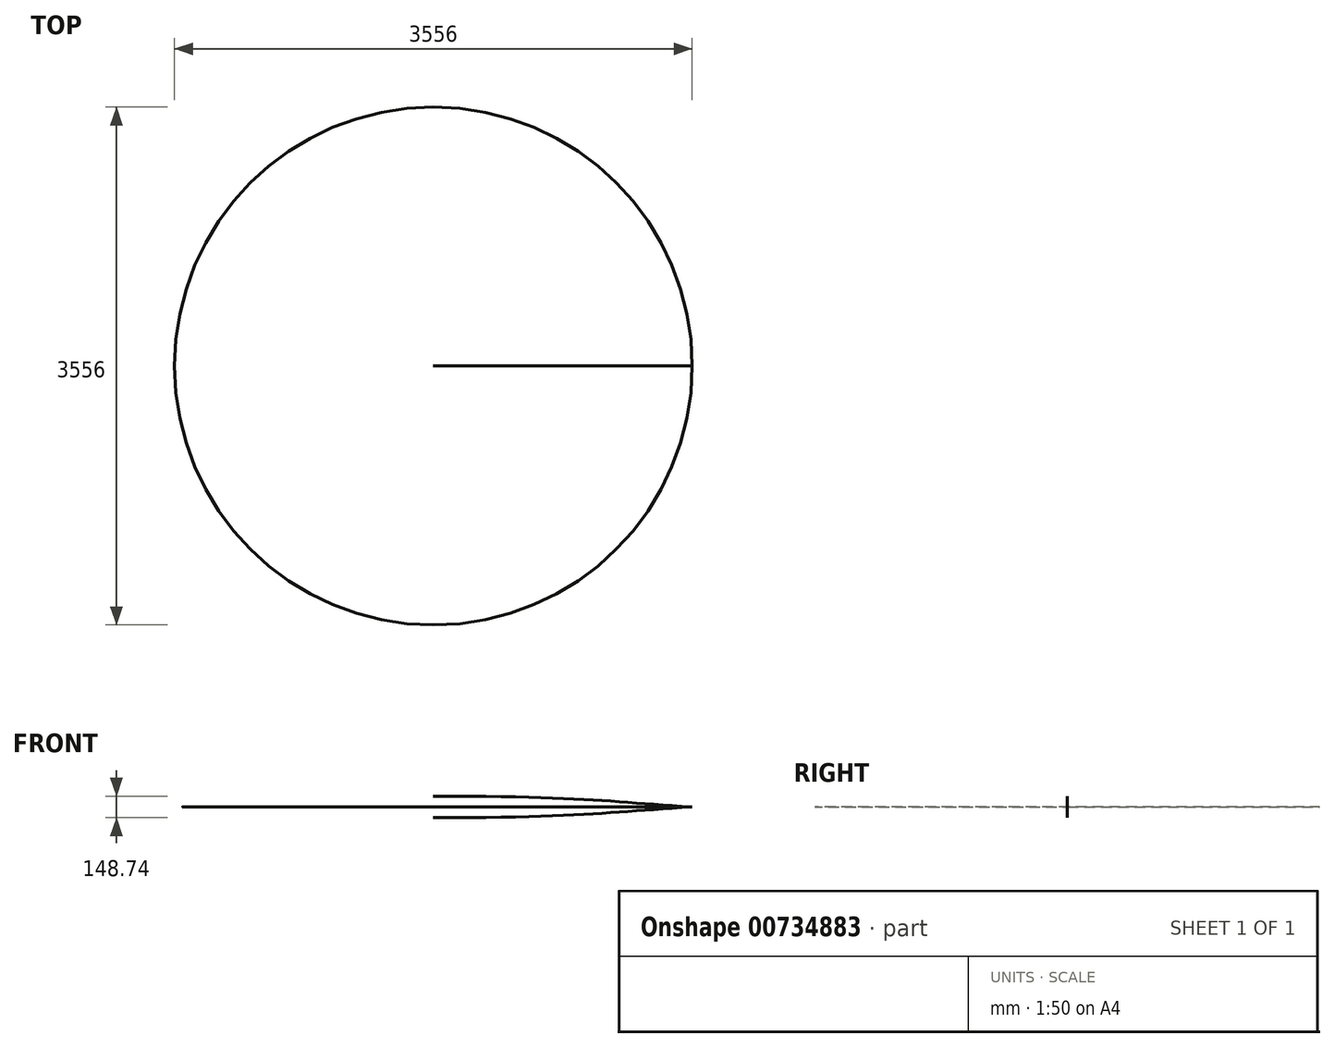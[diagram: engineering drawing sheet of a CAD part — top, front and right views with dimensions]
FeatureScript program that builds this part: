
annotation { "Feature Type Name" : "Feature", "Feature Type Description" : "" }
export const myFeature = defineFeature(function(context is Context, id is Id, definition is map)
    precondition{}
    {
        {
            var Q0;
            Q0=qCreatedBy(makeId("Front.planeOp"),FACE);
            var sketch = newSketch(context, id + "F0", { "sketchPlane" : qUnion([Q0])});
            skLineSegment(sketch, "E0", {"start": v(0, 45.77) * mm, "end": v(0, -49.43) * mm});
            skSolve(sketch);
        }
        {
            var Q0;
            Q0=qCreatedBy(makeId("Front.planeOp"),FACE);
            var sketch = newSketch(context, id + "F1", { "sketchPlane" : qUnion([Q0])});
            skFitSpline(sketch, "E1", {"points": [v(1778, 0) * mm, v(0, 74.37) * mm], "startDerivative": vector(-1668.8, 99.33) * mm, "endDerivative": vector(-3075.44, 0) * mm});
            skFitSpline(sketch, "E2.MirrorCS", {"points": [v(1778, 0) * mm, v(0, -74.37) * mm], "startDerivative": vector(-1668.8, -99.33) * mm, "endDerivative": vector(-3075.44, 0) * mm});
            skLineSegment(sketch, "E3", {"start": v(0, 74.37) * mm, "end": v(0, -74.37) * mm});
            skSolve(sketch);
        }
        {
            var Q0;
            Q0=makeQuery(id+"F1.imprint","IMPRINT",FACE,{"disambiguationData":[TD([[makeQuery(id+"F1.imprint","IMPRINT",EDGE,{"derivedFrom":sQuery(id+"F1.wireOp",EDGE,"E1")}),1.0]])]});
            var Q1;
            Q1=sQuery(id+"F1.wireOp",EDGE,"E1");
            var Q2;
            Q2=sQuery(id+"F1.wireOp",EDGE,"E2.MirrorCS");
            var Q3;
            Q3=sQuery(id+"F0.wireOp",EDGE,"E0");
            revolve(context, id + "F2", {"surfaceOperationType" : NewSurfaceOperationType.NEW, "entities" : qUnion([Q0]), "surfaceEntities" : qUnion([Q1, Q2]), "axis" : qUnion([Q3]), "revolveType" : RevolveType.FULL});
        }
        {
            var Q0;
            Q0=qCreatedBy(makeId("Top.planeOp"),FACE);
            var sketch = newSketch(context, id + "F3", { "sketchPlane" : qUnion([Q0])});
            skLineSegment(sketch, "E4", {"start": v(0, 1845.71) * mm, "end": v(0, -1890.02) * mm, "construction": true});
            skLineSegment(sketch, "E5", {"start": v(0, 0) * mm, "end": v(1614.14, 931.92) * mm, "construction": true});
            skLineSegment(sketch, "E6", {"start": v(0, 0) * mm, "end": v(-1636.2, 944.66) * mm, "construction": true});
            skCircle(sketch, "E7", {"center": v(-1530.34, 883.54) * mm, "radius": 5.63 * mm});
            skCircle(sketch, "E8.1.0", {"center": v(0, -1767.08) * mm, "radius": 5.63 * mm});
            skCircle(sketch, "E8.2.0", {"center": v(1530.34, 883.54) * mm, "radius": 5.63 * mm});
            skPoint(sketch, "E8.center", {"position": v(0, 0) * mm});
            skSolve(sketch);
        }
        {
            var Q0;
            Q0 = qConstructionFilter(qBodyType(qCreatedBy(id + "F3" ,EDGE), BodyType.WIRE), ConstructionObject.NO);
            extrude(context, id + "F4", {"bodyType" : ToolBodyType.SURFACE, "surfaceEntities" : qUnion([Q0]), "depth" : 25400 * mm, "offsetDistance" : 25.4 * mm});
        }
    });
